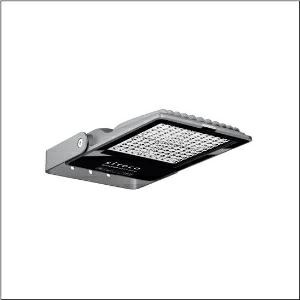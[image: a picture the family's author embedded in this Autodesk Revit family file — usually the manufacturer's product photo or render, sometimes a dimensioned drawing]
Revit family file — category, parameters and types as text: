
# Revit family: sicompact_r__31_mini___pl32_5xa7571c1k23_a489
name_source: partatom
category: Lighting Fixtures
units: mm (PartAtom-declared; Revit-internal decimal feet)

## family parameters
Cut with Voids When Loaded = No
Host = Face
Light Source = No
Part Type = Normal
Room Calculation Point = No
Round Connector Dimension = Use Diameter
Shared = No

## types (1)
- SiCompact® 31 mini  PL32 (1 x LED, 15000 lm, 100 W, 3000K)
    Apparent Load = 100 VA
    CIE Flux Codes = 32 69 98 100 100
    Color Rendering = 70
    Color Temperature = 3000K
    Default Elevation = 1800 mm
    Description = SiCompact® 31 mini, floodlight, primary light control with lens, of plastic, of toughened safety glass, transparent, light distribution: PL32, light emission: direct distribution, primary light characteristic: asymmetric, installation type: surface-mounted, LED, High Power LED, rated luminous flux: 15.000lm, luminous efficacy: 150lm/W, light colour: 730, colour temperature: 3000K, control gear: ECG, with cable, 3x 1.5mm², mains connection: 220..240V, AC, 50/60Hz, connection cable pre-assembled, cable length: 2m, rated input power: 100W, of diecast aluminium, specular, metallic grey (RAL 9006), length: 461mm, width: 261mm, height: 62mm, bracket, of sheet steel, coated, metallic grey (RAL 9006), ON/OFF, protection rating (complete): IP66, insulation class (complete): insulation class I (protective earthing), certification: CE, ENEC, impact resistance: IK08, permissible operating ambient temperature: -40..+45°C, packaging unit: 1 piece

Light Distribution: PL32
    Height = 62 mm  [stored 0.203412 ft]
    Lamp = 1 x LED
    Lamp Light Flux = 15000 lm
    Lamp Power = 100 W
    Lamp count = 1
    Length = 460 mm
    Luminous efficacy = 150 lm/W
    Manufacturer = Siteco
    ModVariant = No
    Model = 5XA7571C1K23
    Mounting Place = Wall
    Mounting Type = Surface mounted
    Number of Poles = 1
    OnlyDefault = Yes
    Power Factor = 1
    Product Name = SiCompact® 31 mini | PL32
    Product group = floodlight | wall mounted
    ProductGroupID = 2001
    Protection Class = Protection class I
    Protection Degree = IP 66
    RLX_Detail_Level = 1
    RLX_Emergency_Light_Flux = 0 lm
    RLX_Emergency_Type = 0
    RLX_Emergency_Type_DB = No
    RlxData = <blob elided: 126701 chars, md5=0b04a344>
    Socket = socket
    Standby Power = 0 W
    System Light Flux = 15000 lm
    System Power = 100 W
    Type Comments = Product without accessories
    Type Image = l_1006951.jpg
    URL = http://relux.com
    VarID = ---
    Voltage = 0 V
    Weight = 0.00 kg
    Width = 260 mm

note: [stored X ft] marks values corroborated as IEEE doubles in the binary element streams (Revit-internal decimal feet)

## geometry (parser evidence)
native form markers: Blend x4, Sweep x15
no freeform markers — native parametric forms only
